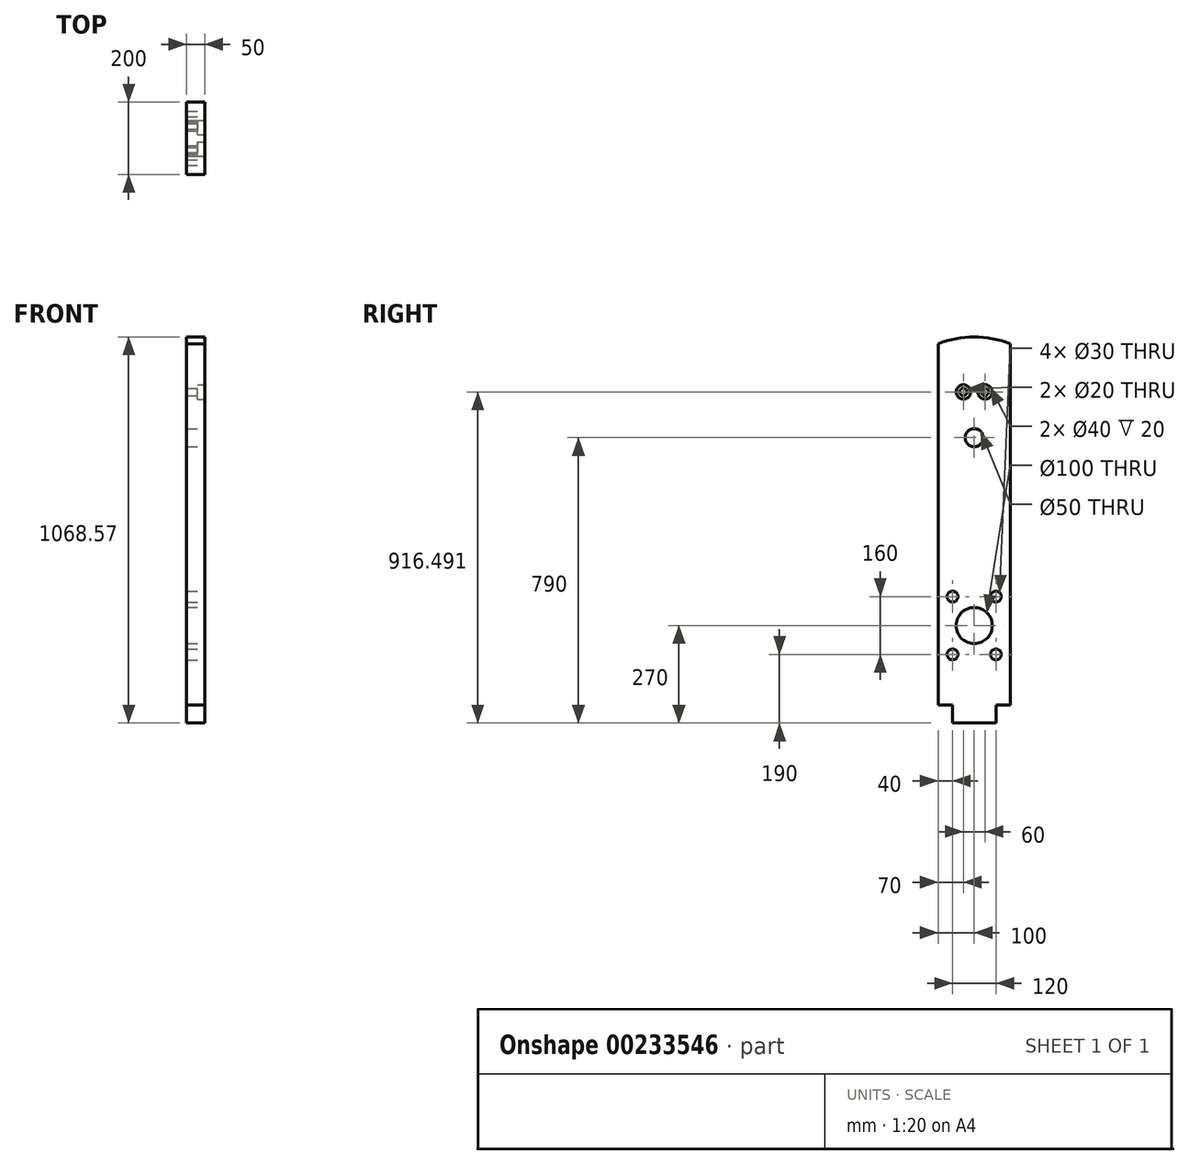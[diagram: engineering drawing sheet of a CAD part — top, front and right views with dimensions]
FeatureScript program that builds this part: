
annotation { "Feature Type Name" : "Feature", "Feature Type Description" : "" }
export const myFeature = defineFeature(function(context is Context, id is Id, definition is map)
    precondition{}
    {
        {
            var Q0;
            Q0=qCreatedBy(makeId("Right.planeOp"),FACE);
            var sketch = newSketch(context, id + "F0", { "sketchPlane" : qUnion([Q0])});
            skLineSegment(sketch, "E0.top", {"start": v(60, -25) * mm, "end": v(-60, -25) * mm});
            skLineSegment(sketch, "E0.left", {"start": v(60, 25) * mm, "end": v(60, -25) * mm});
            skLineSegment(sketch, "E0.right", {"start": v(-60, 25) * mm, "end": v(-60, -25) * mm});
            skPoint(sketch, "E0.middle", {"position": v(0, 0) * mm});
            skLineSegment(sketch, "E1", {"start": v(-60, 25) * mm, "end": v(-100, 25) * mm});
            skLineSegment(sketch, "E2", {"start": v(-100, 25) * mm, "end": v(-100, 1025) * mm});
            skLineSegment(sketch, "E3", {"start": v(100, 1025) * mm, "end": v(100, 25) * mm});
            skLineSegment(sketch, "E4", {"start": v(100, 25) * mm, "end": v(60, 25) * mm});
            skCircle(sketch, "E5", {"center": v(0, 245) * mm, "radius": 50 * mm});
            skPoint(sketch, "E5.centerSnap0", {"position": v(0, -25) * mm});
            skPoint(sketch, "E5.perimeterSnap0", {"position": v(0, -25) * mm});
            skCircle(sketch, "E6", {"center": v(0, 765) * mm, "radius": 25 * mm});
            skArc(sketch, "E7", {"start": v(-100, 848.07) * mm, "mid": v(0, 895) * mm, "end": v(100, 848.07) * mm, "construction": true});
            skArc(sketch, "E8", {"start": v(-100, 1025) * mm, "mid": v(0, 1043.57) * mm, "end": v(100, 1025) * mm});
            skCircle(sketch, "E9", {"center": v(-30, 891.5) * mm, "radius": 10 * mm, "construction": true});
            skLineSegment(sketch, "E10", {"start": v(0, 765) * mm, "end": v(0, 1043.57) * mm, "construction": true});
            skCircle(sketch, "E11.MirrorC", {"center": v(30, 891.5) * mm, "radius": 10 * mm, "construction": true});
            skCircle(sketch, "E12", {"center": v(0, 245) * mm, "radius": 100 * mm, "construction": true});
            skCircle(sketch, "E13", {"center": v(-60, 325) * mm, "radius": 15 * mm, "construction": true});
            skLineSegment(sketch, "E14", {"start": v(0, 424.2) * mm, "end": v(0, 91.12) * mm, "construction": true});
            skLineSegment(sketch, "E15", {"start": v(-100, 245) * mm, "end": v(100, 245) * mm, "construction": true});
            skCircle(sketch, "E16.MirrorC", {"center": v(60, 325) * mm, "radius": 15 * mm, "construction": true});
            skCircle(sketch, "E17.MirrorC", {"center": v(-60, 165) * mm, "radius": 15 * mm, "construction": true});
            skCircle(sketch, "E18.MirrorC", {"center": v(60, 165) * mm, "radius": 15 * mm, "construction": true});
            skSolve(sketch);
        }
        {
            var Q0;
            Q0=makeQuery(id+"F0.imprint","IMPRINT",FACE,{"disambiguationData":[TD([[makeQuery(id+"F0.imprint","IMPRINT",EDGE,{"derivedFrom":sQuery(id+"F0.wireOp",EDGE,"E0.top")}),-1.0]])]});
            extrude(context, id + "F1", {"entities" : qUnion([Q0]), "oppositeDirection" : true, "depth" : 50 * mm});
        }
        {
            var Q0;
            Q0=sQuery(id+"F0.wireOp",VERTEX,"E17.MirrorC.center");
            var Q1;
            Q1=sQuery(id+"F0.wireOp",VERTEX,"E13.center");
            var Q2;
            Q2=sQuery(id+"F0.wireOp",VERTEX,"E16.MirrorC.center");
            var Q3;
            Q3=sQuery(id+"F0.wireOp",VERTEX,"E18.MirrorC.center");
            var Q4;
            Q4=makeQuery(id+"F1.opExtrude","SWEPT_BODY",BODY,{"disambiguationData":[OSD([sQuery(id+"F0.wireOp",EDGE,"E0.top"),sQuery(id+"F0.wireOp",EDGE,"E0.left"),sQuery(id+"F0.wireOp",EDGE,"E0.right"),sQuery(id+"F0.wireOp",EDGE,"E1"),sQuery(id+"F0.wireOp",EDGE,"E2"),sQuery(id+"F0.wireOp",EDGE,"E3"),sQuery(id+"F0.wireOp",EDGE,"E4"),sQuery(id+"F0.wireOp",EDGE,"E5"),sQuery(id+"F0.wireOp",EDGE,"E6"),sQuery(id+"F0.wireOp",EDGE,"E8")])]});
            hole(context, id + "F2", {"style" : HoleStyle.SIMPLE, "endStyle" : HoleEndStyle.THROUGH, "holeDiameter" : 30 * mm, "startFromSketch" : true, "locations" : qUnion([Q0, Q1, Q2, Q3]), "scope" : qUnion([Q4]), "isTappedThrough" : true});
        }
        {
            var Q0;
            Q0=sQuery(id+"F0.wireOp",VERTEX,"E11.MirrorC.center");
            var Q1;
            Q1=sQuery(id+"F0.wireOp",VERTEX,"E9.center");
            var Q2;
            Q2=makeQuery(id+"F1.opExtrude","SWEPT_BODY",BODY,{"disambiguationData":[OSD([sQuery(id+"F0.wireOp",EDGE,"E0.top"),sQuery(id+"F0.wireOp",EDGE,"E0.left"),sQuery(id+"F0.wireOp",EDGE,"E0.right"),sQuery(id+"F0.wireOp",EDGE,"E1"),sQuery(id+"F0.wireOp",EDGE,"E2"),sQuery(id+"F0.wireOp",EDGE,"E3"),sQuery(id+"F0.wireOp",EDGE,"E4"),sQuery(id+"F0.wireOp",EDGE,"E5"),sQuery(id+"F0.wireOp",EDGE,"E6"),sQuery(id+"F0.wireOp",EDGE,"E8")])]});
            hole(context, id + "F3", {"style" : HoleStyle.C_BORE, "endStyle" : HoleEndStyle.THROUGH, "holeDiameter" : 20 * mm, "cBoreDiameter" : 40 * mm, "cBoreDepth" : 20 * mm, "startFromSketch" : true, "locations" : qUnion([Q0, Q1]), "scope" : qUnion([Q2]), "isTappedThrough" : true});
        }
    });
